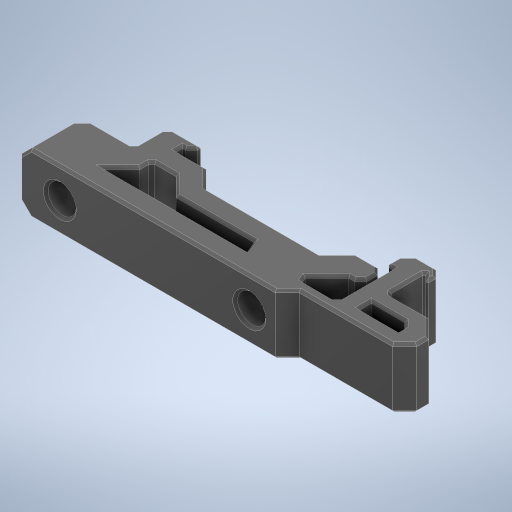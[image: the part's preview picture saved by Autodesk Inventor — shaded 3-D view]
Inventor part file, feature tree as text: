
AUTODESK INVENTOR PART (.ipt)
format: ipt  version: 2023.1 (Build 271208000, 208)  size: 532,992 bytes
history: native  units: mm
features: direct_edit x4, move_body x4, sketch x2, projected_geometry x2, delete_face x1, hole x1, chamfer x1, other x1
ambient origin geometry x8: Origin, YZ Plane, XZ Plane, XY Plane, X Axis, Y Axis, Z Axis, Center Point
bodies: Volumenkörper1 (feature_tree)
feature tree (16):
  direct_edit  "Direktbearbeitung1"
  sketch  "Skizze1"  dims[d0=0.0mm d1=0.0mm d2=2.0mm d3=31.5mm d4=0.0mm d5=0.0mm d6=2.0mm]
  delete_face  "Fläche löschen1"
  direct_edit  "Direktbearbeitung2"
  direct_edit  "Direktbearbeitung3"
  sketch  "Skizze2"  dims[d7=4.7mm d8=4.7mm d9=0.0mm d10=0.0mm d11=31.5mm d12=25.45423mm d13=3.85677mm d14=3.022885mm d15=0.0mm d16=0.0mm d17=1.179291mm d18=3.85677mm d19=0.0mm d20=0.0mm d21=0.2mm d22=3.4mm d23=6.0mm d24=4.7mm d25=5.0mm d26=90.0deg d27=8.0mm d28=90.0deg d29=0.4mm d30=2.0mm d31=45.0deg]
  direct_edit  "Direktbearbeitung4"
  hole  "Bohrung1"  [1 undecoded]
  chamfer  "Fase1"  Distance=2.0mm
  projected_geometry  "Projizierte Kontur1"
  projected_geometry  "Projizierte Kontur2"
  other  "pcb_din_clip_v2"
  move_body  "Verschieben1"
  move_body  "Verschieben2"
  move_body  "Verschieben3"
  move_body  "Verschieben4"
note: 1 required parameter value undecoded (feature->parameter linkage not recoverable at this tier; creation-order binding heuristic only, values carry confidence <= 0.55)
